# Revit family: SDA
name_source: partatom
category: Air Terminals
revit_build: Autodesk Revit 2017 (Build: 20160225_1515(x64)
units: mm (PartAtom-declared; Revit-internal decimal feet)

## family parameters
Always vertical = Yes
Cut with Voids When Loaded = No
Part Type = Normal
Room Calculation Point = No
Round Connector Dimension = Use Diameter
Shared = No
Work Plane-Based = No

## types (8) — shared parameters
Max Flow = 0.0 L/s
Min Flow = 0.0 L/s
Product material = RAL 9016
Schalleistungspegel Lw dB(A) = 30/35/40

## per-type parameters (varying)
| type | A | B | C | D | Druckverlust Δp (Pa) | E | Index | Index1 | Index2 | Visible 1 Stutzen | Visible 2 Reihigem | Visible 2 Stutzen | Visible 3 Stutzen | Visible 4 Stutzen |
| 500_Abmessungen mit 1-reihigem Schlitzauslass | 498 mm  [stored 1.63386 ft] | 27.5 mm  [stored 0.0902231 ft] | 95 mm  [stored 0.31168 ft] | 124.5 mm  [stored 0.408465 ft] | 44/65/91 | 249 mm  [stored 0.816929 ft] | 0 | 1 | 1 | Yes | No | No | No | No |
| 500_Abmessungen mit 2-reihigem Schlitzauslass | 498 mm  [stored 1.63386 ft] | 48.6 mm  [stored 0.159449 ft] | 116 mm  [stored 0.380577 ft] | 124.5 mm  [stored 0.408465 ft] | 34/52/74 | 249 mm  [stored 0.816929 ft] | 1 | 1 | 2 | Yes | Yes | No | No | No |
| 1000_Abmessungen mit 1-reihigem Schlitzauslass | 998 mm  [stored 3.27428 ft] | 27.5 mm  [stored 0.0902231 ft] | 95 mm  [stored 0.31168 ft] | 249.5 mm  [stored 0.81857 ft] | 34/52/74 | 499 mm  [stored 1.63714 ft] | 0 | 2 | 1 | No | No | Yes | No | No |
| 1000_Abmessungen mit 2-reihigem Schlitzauslass | 998 mm  [stored 3.27428 ft] | 48.6 mm  [stored 0.159449 ft] | 116 mm  [stored 0.380577 ft] | 249.5 mm  [stored 0.81857 ft] | 25/40/60 | 499 mm  [stored 1.63714 ft] | 1 | 2 | 2 | No | Yes | No | Yes | No |
| 1500_Abmessungen mit 1-reihigem Schlitzauslass | 1498 mm  [stored 4.9147 ft] | 27.5 mm  [stored 0.0902231 ft] | 95 mm  [stored 0.31168 ft] | 374.5 mm  [stored 1.22867 ft] | 29/45/66 | 749 mm  [stored 2.45735 ft] | 0 | 3 | 1 | No | No | No | Yes | No |
| 1500_Abmessungen mit 2-reihigem Schlitzauslass | 1498 mm  [stored 4.9147 ft] | 48.6 mm  [stored 0.159449 ft] | 116 mm  [stored 0.380577 ft] | 374.5 mm  [stored 1.22867 ft] | 21/35/53 | 749 mm  [stored 2.45735 ft] | 1 | 3 | 2 | No | Yes | No | No | Yes |
| 2000_Abmessungen mit 1-reihigem Schlitzauslass | 1998 mm  [stored 6.55512 ft] | 27.5 mm  [stored 0.0902231 ft] | 95 mm  [stored 0.31168 ft] | 499.5 mm  [stored 1.63878 ft] | 25/40/60 | 999 mm  [stored 3.27756 ft] | 0 | 4 | 1 | No | No | No | No | Yes |
| 2000_Abmessungen mit 2-reihigem Schlitzauslass | 1998 mm  [stored 6.55512 ft] | 48.6 mm  [stored 0.159449 ft] | 116 mm  [stored 0.380577 ft] | 499.5 mm  [stored 1.63878 ft] | 18/31/48 | 999 mm  [stored 3.27756 ft] | 1 | 4 | 2 | No | Yes | No | No | Yes |

note: [stored X ft] marks values corroborated as IEEE doubles in the binary element streams (Revit-internal decimal feet)

## geometry (parser evidence)
native form markers: Sweep x2
no freeform markers — native parametric forms only
